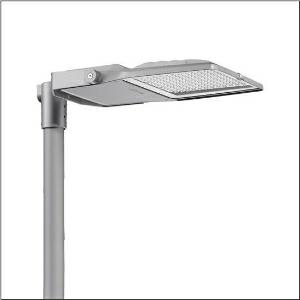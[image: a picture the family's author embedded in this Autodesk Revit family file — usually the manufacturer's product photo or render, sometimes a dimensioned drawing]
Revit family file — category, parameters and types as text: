
# Revit family: floodlight_fl_21_iq_midi___pl52_5xa7782f4d3a_fe87
name_source: partatom
category: Lighting Fixtures
units: mm (PartAtom-declared; Revit-internal decimal feet)

## family parameters
Cut with Voids When Loaded = No
Host = Face
Light Source = No
Part Type = Normal
Room Calculation Point = No
Round Connector Dimension = Use Diameter
Shared = No

## types (1)
- --- (1 x LED, 37330 lm, 270.2 W, 4000K)
    Apparent Load = 270 VA
    CIE Flux Codes = 26 60 98 100 100
    Color Rendering = 70
    Color Temperature = 4000K
    Default Elevation = 1800 mm
    Description = Floodlight FL 21 iQ midi, floodlight, primary light control with lens, of PMMA, primary optical cover: protective disc, of toughened safety glass, transparent, light distribution: PL52, light emission: direct distribution, installation type: surface-mounted, LED, High Power LED, rated luminous flux: 37.330lm, luminous efficacy: 138lm/W, light colour: 740, colour temperature: 4000K, control gear: iQ Street-Remote/DALI, control: optimised constant luminous flux control (CLO 2.0), Desk-Remote (wireless, voltage-free reading and setting of iQ features in the workshop via application-optimized NFC function/RFID function), Smart-Wire, Night-Set, Temp-Guard, Auto-Match, Street-Remote, with terminal, 6-pole, mains connection: 220..240V, AC, 50/60Hz, start of lifetime: 270W, end of service life: 287W, reduction: 118W, luminaire housing, of diecast aluminium, powder-coated, Siteco® metallic grey (DB 702S), corrosivity category C5 mid according to DIN EN ISO 12944, suitable for swimming pools, chlorine-resistant, sealing non-destructively replaceable, please order mast flange separately, mast bracket, of steel, galvanised, powder-coated, Siteco® metallic grey (DB 702S), protection rating (complete): IP66, insulation class (complete): insulation class II (safety insulation), certification: CE, ENEC, VDE, protection symbol: D, impact resistance: IK08, permissible operating ambient temperature: -40..+40°C, permissible operating ambient temperature for outdoor applications: -40..+50°C, standard: DIN EN 12944, LABS conformity tested according to VDMA 24364:2018-05, packaging unit: 1 piece

Light Distribution: PL52
    Height = 76 mm
    Lamp = 1 x LED
    Lamp Light Flux = 37330 lm
    Lamp Power = 270.2 W
    Lamp count = 1
    Length = 657 mm
    Luminous efficacy = 138 lm/W
    Manufacturer = Siteco
    ModVariant = No
    Model = 5XA7782F4D3A
    Number of Poles = 1
    OnlyDefault = Yes
    Power Factor = 1
    Product Name = Floodlight FL 21 iQ midi | PL52
    Product group = floodlight | pylon annexe
    ProductGroupID = 6200
    Protection Class = Protection class II
    Protection Degree = IP 66
    RLX_Detail_Level = 1
    RLX_Emergency_Light_Flux = 0 lm
    RLX_Emergency_Type = 0
    RLX_Emergency_Type_DB = No
    RlxData = <blob elided: 153913 chars, md5=40387072>
    Socket = socket
    Standby Power = 0 W
    System Light Flux = 37330 lm
    System Power = 270 W
    Type Comments = factory setting: luminous flux: 100 % | dim-lin: 254 | 620 mA
    Type Image = l_1007123.jpg
    URL = http://relux.com
    VarID = @adj_105522
    Voltage = 0 V
    Weight = 0.00 kg
    Width = 442 mm

## geometry (parser evidence)
native form markers: Blend x4, Sweep x15
no freeform markers — native parametric forms only
